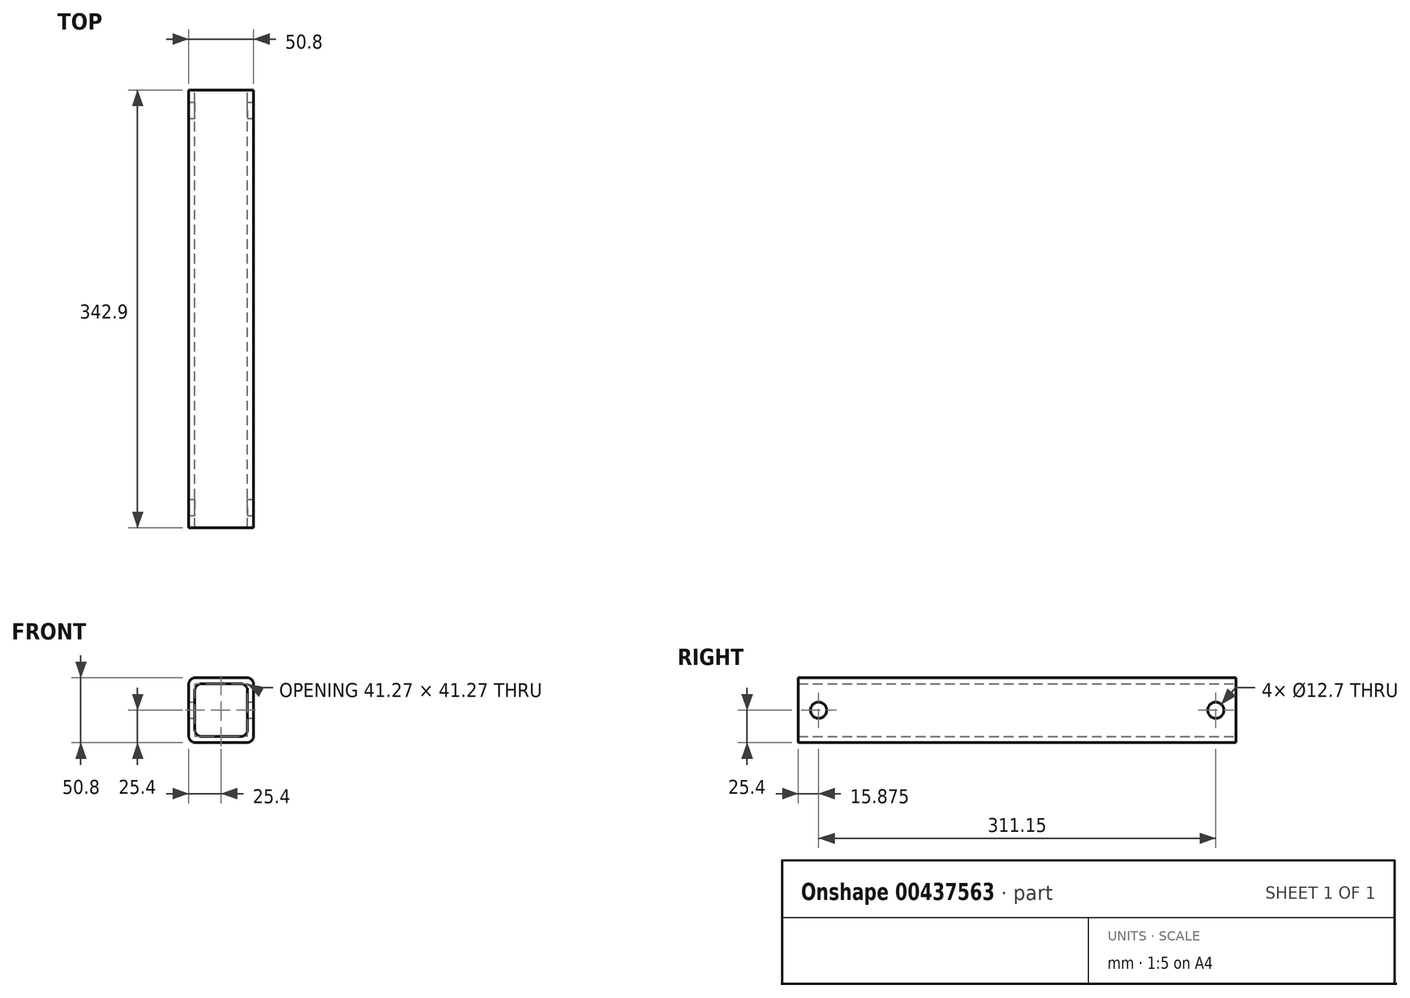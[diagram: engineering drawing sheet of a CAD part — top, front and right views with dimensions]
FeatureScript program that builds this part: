
annotation { "Feature Type Name" : "Feature", "Feature Type Description" : "" }
export const myFeature = defineFeature(function(context is Context, id is Id, definition is map)
    precondition{}
    {
        {
            var Q0;
            Q0=qCreatedBy(makeId("Front.planeOp"),FACE);
            var sketch = newSketch(context, id + "F0", { "sketchPlane" : qUnion([Q0])});
            skLineSegment(sketch, "E0.bottom", {"start": v(25.4, -25.4) * mm, "end": v(-25.4, -25.4) * mm});
            skLineSegment(sketch, "E0.top", {"start": v(25.4, 25.4) * mm, "end": v(-25.4, 25.4) * mm});
            skLineSegment(sketch, "E0.left", {"start": v(25.4, -25.4) * mm, "end": v(25.4, 25.4) * mm});
            skLineSegment(sketch, "E0.right", {"start": v(-25.4, -25.4) * mm, "end": v(-25.4, 25.4) * mm});
            skPoint(sketch, "E0.middle", {"position": v(0, 0) * mm});
            skLineSegment(sketch, "E1.bottom", {"start": v(20.64, -20.64) * mm, "end": v(-20.64, -20.64) * mm});
            skLineSegment(sketch, "E1.top", {"start": v(20.64, 20.64) * mm, "end": v(-20.64, 20.64) * mm});
            skLineSegment(sketch, "E1.left", {"start": v(20.64, -20.64) * mm, "end": v(20.64, 20.64) * mm});
            skLineSegment(sketch, "E1.right", {"start": v(-20.64, -20.64) * mm, "end": v(-20.64, 20.64) * mm});
            skSolve(sketch);
        }
        {
            var Q0;
            Q0 = qSketchRegion(id + "F0", true);
            extrude(context, id + "F1", {"entities" : qUnion([Q0]), "endBound" : BoundingType.SYMMETRIC, "depth" : 342.9 * mm});
        }
        {
            var Q0;
            Q0=makeQuery(id+"F1.opExtrude","SWEPT_EDGE",EDGE,{"disambiguationData":[OSD([sQuery(id+"F0.wireOp",EDGE,"E1.top"),sQuery(id+"F0.wireOp",EDGE,"E1.right")])]});
            var Q1;
            Q1=makeQuery(id+"F1.opExtrude","SWEPT_EDGE",EDGE,{"disambiguationData":[OSD([sQuery(id+"F0.wireOp",EDGE,"E0.bottom"),sQuery(id+"F0.wireOp",EDGE,"E0.left")])]});
            var Q2;
            Q2=makeQuery(id+"F1.opExtrude","SWEPT_EDGE",EDGE,{"disambiguationData":[OSD([sQuery(id+"F0.wireOp",EDGE,"E0.bottom"),sQuery(id+"F0.wireOp",EDGE,"E0.right")])]});
            var Q3;
            Q3=makeQuery(id+"F1.opExtrude","SWEPT_EDGE",EDGE,{"disambiguationData":[OSD([sQuery(id+"F0.wireOp",EDGE,"E0.top"),sQuery(id+"F0.wireOp",EDGE,"E0.left")])]});
            var Q4;
            Q4=makeQuery(id+"F1.opExtrude","SWEPT_EDGE",EDGE,{"disambiguationData":[OSD([sQuery(id+"F0.wireOp",EDGE,"E1.bottom"),sQuery(id+"F0.wireOp",EDGE,"E1.left")])]});
            var Q5;
            Q5=makeQuery(id+"F1.opExtrude","SWEPT_EDGE",EDGE,{"disambiguationData":[OSD([sQuery(id+"F0.wireOp",EDGE,"E0.top"),sQuery(id+"F0.wireOp",EDGE,"E0.right")])]});
            var Q6;
            Q6=makeQuery(id+"F1.opExtrude","SWEPT_EDGE",EDGE,{"disambiguationData":[OSD([sQuery(id+"F0.wireOp",EDGE,"E1.top"),sQuery(id+"F0.wireOp",EDGE,"E1.left")])]});
            var Q7;
            Q7=makeQuery(id+"F1.opExtrude","SWEPT_EDGE",EDGE,{"disambiguationData":[OSD([sQuery(id+"F0.wireOp",EDGE,"E1.bottom"),sQuery(id+"F0.wireOp",EDGE,"E1.right")])]});
            fillet(context, id + "F2", {"entities" : qUnion([Q0, Q1, Q2, Q3, Q4, Q5, Q6, Q7]), "radius" : 5.08 * mm, "tangentPropagation" : true, "allowEdgeOverflow" : false});
        }
        {
            var Q0;
            Q0=makeQuery(id+"F1.opExtrude","SWEPT_FACE",FACE,{"disambiguationData":[OSD([sQuery(id+"F0.wireOp",EDGE,"E0.left")])]});
            var sketch = newSketch(context, id + "F3", { "sketchPlane" : qUnion([Q0])});
            skCircle(sketch, "E2", {"center": v(-155.58, 0) * mm, "radius": 6.35 * mm});
            skPoint(sketch, "E2.centerSnap0", {"position": v(-171.45, 0) * mm});
            skCircle(sketch, "E3.MirrorC", {"center": v(155.58, 0) * mm, "radius": 6.35 * mm});
            skSolve(sketch);
        }
        {
            var Q0;
            Q0 = qSketchRegion(id + "F3", true);
            extrude(context, id + "F4", {"entities" : qUnion([Q0]), "operationType" : NewBodyOperationType.REMOVE, "endBound" : BoundingType.THROUGH_ALL, "oppositeDirection" : true, "depth" : 50.8 * mm});
        }
    });
